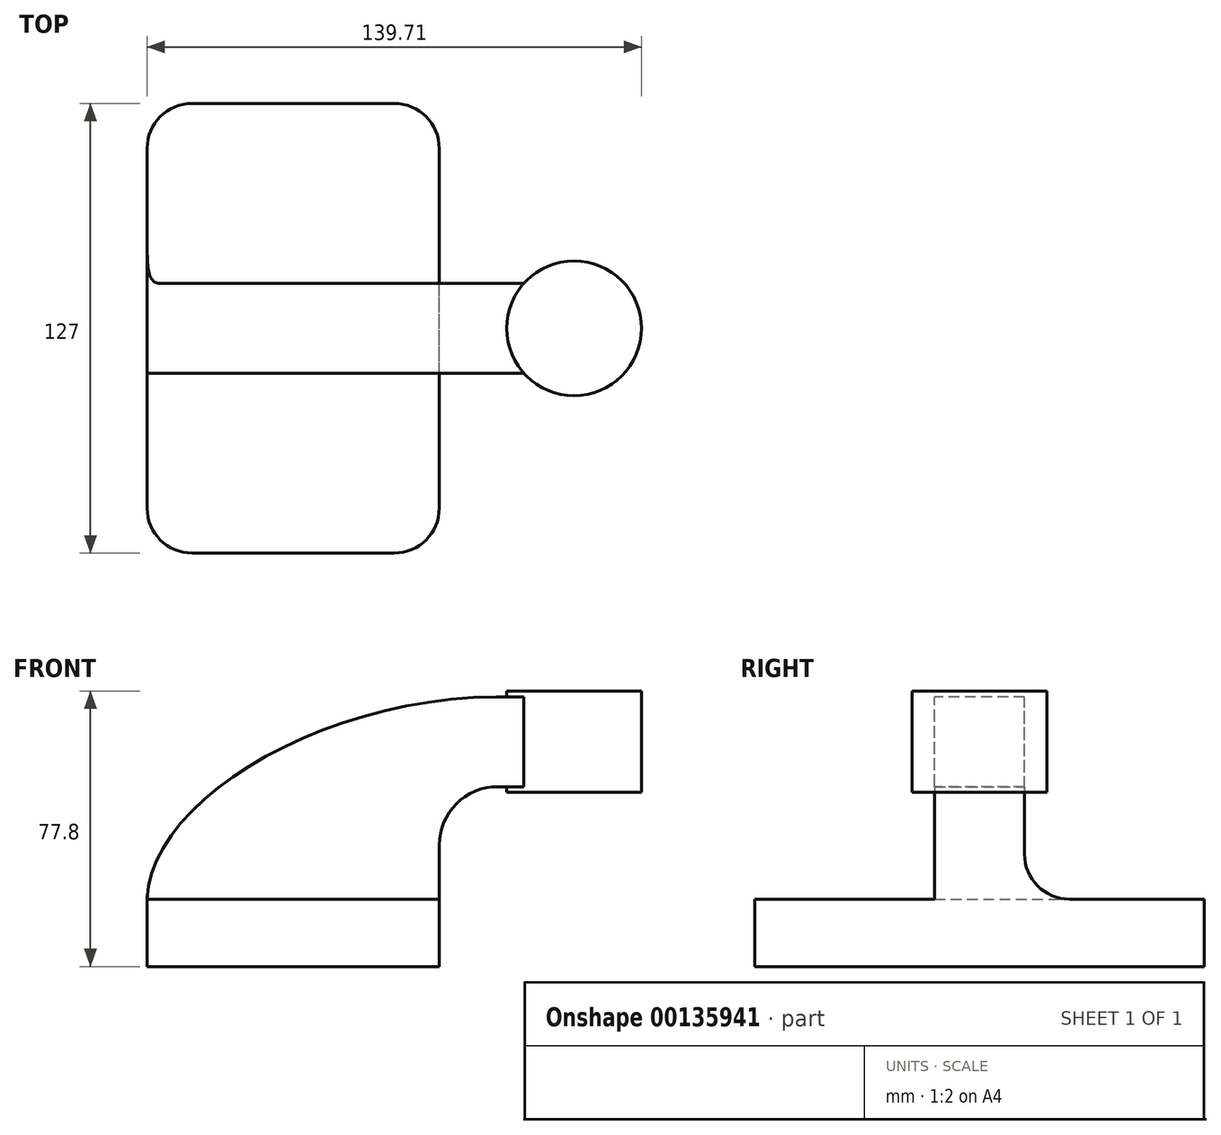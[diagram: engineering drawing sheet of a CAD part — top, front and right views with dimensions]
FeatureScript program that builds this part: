
annotation { "Feature Type Name" : "Feature", "Feature Type Description" : "" }
export const myFeature = defineFeature(function(context is Context, id is Id, definition is map)
    precondition{}
    {
        {
            var Q0;
            Q0=qCreatedBy(makeId("Front.planeOp"),FACE);
            var sketch = newSketch(context, id + "F0", { "sketchPlane" : qUnion([Q0])});
            skLineSegment(sketch, "E0.bottom", {"start": v(41.27, 9.53) * mm, "end": v(-41.28, 9.53) * mm});
            skLineSegment(sketch, "E0.top", {"start": v(41.28, -9.52) * mm, "end": v(-41.27, -9.52) * mm});
            skLineSegment(sketch, "E0.left", {"start": v(41.28, 9.53) * mm, "end": v(41.28, -9.52) * mm});
            skLineSegment(sketch, "E0.right", {"start": v(-41.28, 9.53) * mm, "end": v(-41.27, -9.52) * mm});
            skPoint(sketch, "E0.middle", {"position": v(0, 0) * mm});
            skLineSegment(sketch, "E1.bottom", {"start": v(98.42, 68.27) * mm, "end": v(60.32, 68.27) * mm});
            skLineSegment(sketch, "E1.top", {"start": v(98.42, 39.7) * mm, "end": v(60.32, 39.7) * mm});
            skLineSegment(sketch, "E1.left", {"start": v(98.42, 68.27) * mm, "end": v(98.42, 39.7) * mm});
            skLineSegment(sketch, "E1.right", {"start": v(60.33, 68.27) * mm, "end": v(60.33, 39.7) * mm});
            skPoint(sketch, "E1.middle", {"position": v(79.38, 53.98) * mm});
            skLineSegment(sketch, "E2", {"start": v(41.27, 9.53) * mm, "end": v(41.27, 24.77) * mm});
            skArc(sketch, "E3", {"start": v(41.27, 24.77) * mm, "mid": v(46.11, 36.44) * mm, "end": v(57.79, 41.28) * mm});
            skLineSegment(sketch, "E4", {"start": v(57.79, 41.28) * mm, "end": v(79.38, 41.28) * mm});
            skLineSegment(sketch, "E5.0", {"start": v(57.79, 66.68) * mm, "end": v(79.38, 66.68) * mm});
            skArc(sketch, "E5.1", {"start": v(15.88, 24.77) * mm, "mid": v(28.15, 54.4) * mm, "end": v(57.79, 66.68) * mm});
            skLineSegment(sketch, "E5.2", {"start": v(15.87, 9.53) * mm, "end": v(15.87, 24.77) * mm});
            skFitSpline(sketch, "E6", {"points": [v(-41.28, 9.52) * mm, v(57.79, 66.68) * mm], "startDerivative": vector(2.62, 83.83) * mm, "endDerivative": vector(148.51, 0.52) * mm});
            skLineSegment(sketch, "E7", {"start": v(79.38, 66.68) * mm, "end": v(79.38, 41.28) * mm});
            skLineSegment(sketch, "E8", {"start": v(79.37, 68.27) * mm, "end": v(79.37, 39.7) * mm});
            skSolve(sketch);
        }
        {
            var Q0;
            Q0=makeQuery(id+"F0.imprint","IMPRINT",FACE,{"disambiguationData":[TD([[makeQuery(id+"F0.imprint","IMPRINT",EDGE,{"derivedFrom":sQuery(id+"F0.wireOp",EDGE,"E0.top")}),-1.0]])]});
            extrude(context, id + "F1", {"entities" : qUnion([Q0]), "endBound" : BoundingType.SYMMETRIC, "depth" : 127 * mm});
        }
        {
            var Q0;
            {var subQ3=sQuery(id+"F0.wireOp",EDGE,"E5.2");Q0=makeQuery(id+"F0.imprint","IMPRINT",FACE,{"disambiguationData":[TD([[makeQuery(id+"F0.imprint","IMPRINT",EDGE,{"derivedFrom":subQ3}),1.0]])]});}
            var Q1;
            {var subQ1=sQuery(id+"F0.wireOp",EDGE,"E2");Q1=makeQuery(id+"F0.imprint","IMPRINT",FACE,{"disambiguationData":[TD([[makeQuery(id+"F0.imprint","IMPRINT",EDGE,{"derivedFrom":subQ1}),1.0]])]});}
            var Q2;
            {var subQ5=sQuery(id+"F0.wireOp",EDGE,"E7");Q2=makeQuery(id+"F0.imprint","IMPRINT",FACE,{"disambiguationData":[TD([[makeQuery(id+"F0.imprint","IMPRINT",EDGE,{"derivedFrom":subQ5}),-1.0]])]});}
            var Q3;
            {var subQ0=sQuery(id+"F0.wireOp",EDGE,"E5.0");var subQ1=sQuery(id+"F0.wireOp",EDGE,"E1.right");var subQ2=makeQuery(id+"F0.imprint","INTERSECT",VERTEX,{"derivedFrom":[subQ1,subQ0]});Q3=makeQuery(id+"F0.imprint","IMPRINT",FACE,{"disambiguationData":[TD([[makeQuery(id+"F0.imprint","IMPRINT",EDGE,{"disambiguationData":[TD([[subQ2,-1.0]])],"derivedFrom":subQ1}),1.0]])]});}
            extrude(context, id + "F2", {"entities" : qUnion([Q0, Q1, Q2, Q3]), "operationType" : NewBodyOperationType.ADD, "endBound" : BoundingType.SYMMETRIC, "depth" : 25.4 * mm});
        }
        {
            var Q0;
            {var subQ4=sQuery(id+"F0.wireOp",EDGE,"E1.left");Q0=makeQuery(id+"F0.imprint","IMPRINT",FACE,{"disambiguationData":[TD([[makeQuery(id+"F0.imprint","IMPRINT",EDGE,{"derivedFrom":subQ4}),-1.0]])]});}
            var Q1;
            Q1=sQuery(id+"F0.wireOp",EDGE,"E8");
            revolve(context, id + "F3", {"operationType" : NewBodyOperationType.ADD, "entities" : qUnion([Q0]), "axis" : qUnion([Q1]), "revolveType" : RevolveType.FULL});
        }
        {
            var Q0;
            Q0=makeQuery(id+"F1.opExtrude","CAP_EDGE",EDGE,{"disambiguationData":[OSD([sQuery(id+"F0.wireOp",EDGE,"E0.left")])],"isStart":false});
            var Q1;
            Q1=makeQuery(id+"F1.opExtrude","CAP_EDGE",EDGE,{"disambiguationData":[OSD([sQuery(id+"F0.wireOp",EDGE,"E0.right")])],"isStart":false});
            var Q2;
            Q2=makeQuery(id+"F1.opExtrude","CAP_EDGE",EDGE,{"disambiguationData":[OSD([sQuery(id+"F0.wireOp",EDGE,"E0.right")])],"isStart":true});
            var Q3;
            Q3=makeQuery(id+"F1.opExtrude","CAP_EDGE",EDGE,{"disambiguationData":[OSD([sQuery(id+"F0.wireOp",EDGE,"E0.left")])],"isStart":true});
            var Q4;
            Q4=makeQuery(id+"F2.opExtrude","CAP_EDGE",EDGE,{"disambiguationData":[OSD([sQuery(id+"F0.wireOp",EDGE,"E0.bottom")])],"isStart":true});
            var Q5;
            Q5=makeQuery(id+"F2.opExtrude","CAP_EDGE",EDGE,{"disambiguationData":[OSD([sQuery(id+"F0.wireOp",EDGE,"E0.bottom")])],"isStart":false});
            fillet(context, id + "F4", {"entities" : qUnion([Q0, Q1, Q2, Q3, Q4, Q5]), "radius" : 12.7 * mm, "tangentPropagation" : true, "allowEdgeOverflow" : false});
        }
    });
